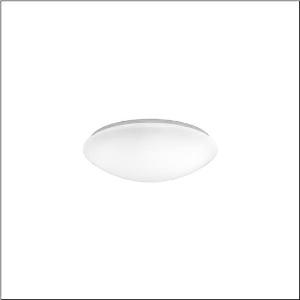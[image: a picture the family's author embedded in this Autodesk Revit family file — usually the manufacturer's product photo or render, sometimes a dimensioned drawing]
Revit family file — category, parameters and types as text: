
# Revit family: round_31_b_5pja032001a
name_source: partatom
category: Lighting Fixtures
units: mm (PartAtom-declared; Revit-internal decimal feet)

## family parameters
Cut with Voids When Loaded = No
Host = Face
Light Source = No
Part Type = Normal
Room Calculation Point = No
Round Connector Dimension = Use Diameter
Shared = No

## types (1)
- Round 31 B (1 x LED, 1900 lm, 15 W, 4000K)
    Apparent Load = 15 VA
    CIE Flux Codes = 42 71 89 88 100
    Color Rendering = 80
    Color Temperature = 4000K
    Default Elevation = 1800 mm
    Description = Round 31 B, wall and ceiling luminaire, primary optical cover: enclosure, of PMMA, light emission: direct distribution, primary light characteristic: symmetric, installation type: surface-mounted, LED, rated luminous flux: 1.900lm, luminous efficacy: 126lm/W, light colour: 840, colour temperature: 4000K, with terminal, 3+2-pole, max. 2.5mm², mains connection: 230V, AC, 50/60Hz, rated input power: 15W, luminaire housing, round, of steel, white, diameter: 290mm, height: 85mm, protection rating (complete): IP40, insulation class (complete): insulation class I (protective earthing), certification: CE, impact resistance: IK02, packaging unit: 1 piece
    Height = 85 mm
    Lamp = 1 x LED
    Lamp Light Flux = 1900 lm
    Lamp Power = 15 W
    Lamp count = 1
    Length = 290 mm
    Luminous efficacy = 127 lm/W
    Manufacturer = Siteco
    ModVariant = No
    Model = 5PJA032001A
    Mounting Place = Ceiling
    Mounting Type = Surface mounted
    Number of Poles = 1
    OnlyDefault = Yes
    Power Factor = 1
    Product Name = Round 31 B
    Product group = wall and ceiling luminaire
    ProductGroupID = 302
    Protection Class = Protection class I
    Protection Degree = IP 40
    RLX_Detail_Level = 1
    RLX_Emergency_Light_Flux = 0 lm
    RLX_Emergency_Type = 0
    RLX_Emergency_Type_DB = No
    RlxData = <blob elided: 9181 chars, md5=6b81a242>
    Socket = socket
    Standby Power = 0 W
    System Light Flux = 1900 lm
    System Power = 15 W
    Type Comments = Product without accessories
    Type Image = l_1258346.jpg
    URL = http://relux.com
    VarID = ---
    Voltage = 0 V
    Weight = 0.00 kg
    Width = 0 mm  [stored 0 ft]

note: [stored X ft] marks values corroborated as IEEE doubles in the binary element streams (Revit-internal decimal feet)

## geometry (parser evidence)
native form markers: Sweep x10
no freeform markers — native parametric forms only
